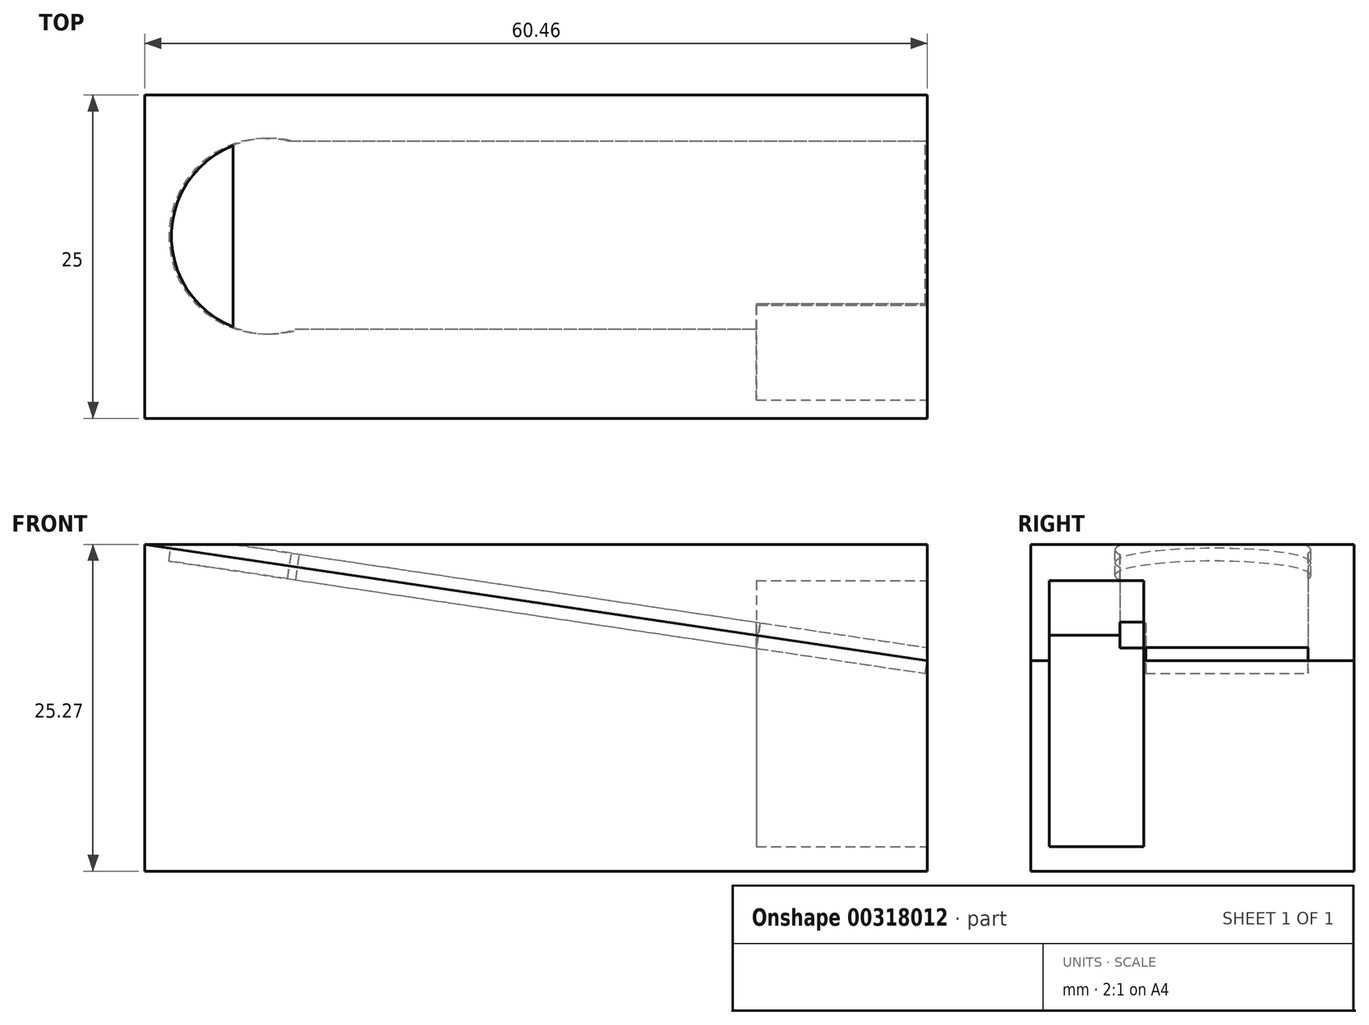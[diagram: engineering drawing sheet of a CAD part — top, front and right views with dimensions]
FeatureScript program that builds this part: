
annotation { "Feature Type Name" : "Feature", "Feature Type Description" : "" }
export const myFeature = defineFeature(function(context is Context, id is Id, definition is map)
    precondition{}
    {
        {
            var Q0;
            Q0=qCreatedBy(makeId("Front.planeOp"),FACE);
            var sketch = newSketch(context, id + "F0", { "sketchPlane" : qUnion([Q0])});
            skLineSegment(sketch, "E0.bottom", {"start": v(0, 0) * mm, "end": v(-60.46, 0) * mm});
            skLineSegment(sketch, "E0.top", {"start": v(0, 25.27) * mm, "end": v(-60.46, 25.27) * mm});
            skLineSegment(sketch, "E0.left", {"start": v(0, 0) * mm, "end": v(0, 25.27) * mm});
            skLineSegment(sketch, "E0.right", {"start": v(-60.46, 0) * mm, "end": v(-60.46, 25.27) * mm});
            skSolve(sketch);
        }
        {
            var Q0;
            Q0=makeQuery(id+"F0.imprint","IMPRINT",FACE,{"disambiguationData":[TD([[makeQuery(id+"F0.imprint","IMPRINT",EDGE,{"derivedFrom":sQuery(id+"F0.wireOp",EDGE,"E0.bottom")}),-1.0]])]});
            extrude(context, id + "F1", {"entities" : qUnion([Q0]), "depth" : 25 * mm});
        }
        {
            var Q0;
            Q0=makeQuery(id+"F1.opExtrude","SWEPT_FACE",FACE,{"disambiguationData":[OSD([sQuery(id+"F0.wireOp",EDGE,"E0.left")])]});
            var sketch = newSketch(context, id + "F2", { "sketchPlane" : qUnion([Q0])});
            skLineSegment(sketch, "E1.bottom", {"start": v(-25, 16.28) * mm, "end": v(0, 16.28) * mm});
            skLineSegment(sketch, "E1.top", {"start": v(-25, 0) * mm, "end": v(0, 0) * mm});
            skLineSegment(sketch, "E1.left", {"start": v(-25, 16.28) * mm, "end": v(-25, 0) * mm});
            skLineSegment(sketch, "E1.right", {"start": v(0, 16.28) * mm, "end": v(0, 0) * mm});
            skSolve(sketch);
        }
        {
            var Q0;
            Q0=makeQuery(id+"F1.opExtrude","SWEPT_FACE",FACE,{"disambiguationData":[OSD([sQuery(id+"F0.wireOp",EDGE,"E0.right")])]});
            var sketch = newSketch(context, id + "F3", { "sketchPlane" : qUnion([Q0])});
            skLineSegment(sketch, "E2.bottom", {"start": v(0, 25.27) * mm, "end": v(25, 25.27) * mm});
            skLineSegment(sketch, "E2.top", {"start": v(0, 0) * mm, "end": v(25, 0) * mm});
            skLineSegment(sketch, "E2.left", {"start": v(0, 25.27) * mm, "end": v(0, 0) * mm});
            skLineSegment(sketch, "E2.right", {"start": v(25, 25.27) * mm, "end": v(25, 0) * mm});
            skSolve(sketch);
        }
        {
            var Q1;
            Q1 = qSketchRegion(id + "F2", true);
            var Q2;
            Q2 = qSketchRegion(id + "F3", true);
            loft(context, id + "F4", {"sheetProfilesArray" : [{ "sheetProfileEntities" : qUnion([Q1]) }, { "sheetProfileEntities" : qUnion([Q2]) }]});
        }
        {
            var Q0;
            Q0=makeQuery(id+"F4.opLoft","SWEPT_FACE",FACE,{"disambiguationData":[OSD([sQuery(id+"F0.wireOp",EDGE,"E0.left"),sQuery(id+"F2.wireOp",EDGE,"E1.bottom"),sQuery(id+"F2.wireOp",EDGE,"E1.left"),sQuery(id+"F2.wireOp",EDGE,"E1.right"),sQuery(id+"F3.wireOp",EDGE,"E2.bottom"),sQuery(id+"F3.wireOp",EDGE,"E2.left"),sQuery(id+"F3.wireOp",EDGE,"E2.right")])]});
            var sketch = newSketch(context, id + "F5", { "sketchPlane" : qUnion([Q0])});
            skArc(sketch, "E3", {"start": v(-52.21, -3.54) * mm, "mid": v(-61.5, -11.24) * mm, "end": v(-51.58, -18.1) * mm});
            skLineSegment(sketch, "E4", {"start": v(-52.21, -3.54) * mm, "end": v(-2.4, -3.54) * mm});
            skLineSegment(sketch, "E5", {"start": v(-51.58, -18.1) * mm, "end": v(-15.6, -18.1) * mm});
            skLineSegment(sketch, "E6", {"start": v(-15.6, -18.1) * mm, "end": v(-15.6, -16.11) * mm});
            skLineSegment(sketch, "E7", {"start": v(-15.6, -16.11) * mm, "end": v(-2.4, -16.11) * mm});
            skSolve(sketch);
        }
        {
            var Q0;
            Q0=makeQuery(id+"F5.imprint","IMPRINT",FACE,{"disambiguationData":[TD([[makeQuery(id+"F5.imprint","IMPRINT",EDGE,{"derivedFrom":sQuery(id+"F5.wireOp",EDGE,"E3")}),1.0]])]});
            extrude(context, id + "F6", {"entities" : qUnion([Q0]), "operationType" : NewBodyOperationType.REMOVE, "endBound" : BoundingType.SYMMETRIC, "oppositeDirection" : true, "depth" : 2 * mm});
        }
        {
            var Q0;
            Q0=qCreatedBy(makeId("Right.planeOp"),FACE);
            var sketch = newSketch(context, id + "F7", { "sketchPlane" : qUnion([Q0])});
            skLineSegment(sketch, "E8.bottom", {"start": v(-16.26, 22.48) * mm, "end": v(-23.57, 22.48) * mm});
            skLineSegment(sketch, "E8.top", {"start": v(-16.26, 1.89) * mm, "end": v(-23.57, 1.89) * mm});
            skLineSegment(sketch, "E8.left", {"start": v(-16.26, 22.48) * mm, "end": v(-16.26, 1.89) * mm});
            skLineSegment(sketch, "E8.right", {"start": v(-23.57, 22.48) * mm, "end": v(-23.57, 1.89) * mm});
            skSolve(sketch);
        }
        {
            var Q0;
            Q0=makeQuery(id+"F7.imprint","IMPRINT",FACE,{"disambiguationData":[TD([[makeQuery(id+"F7.imprint","IMPRINT",EDGE,{"derivedFrom":sQuery(id+"F7.wireOp",EDGE,"E8.bottom")}),1.0]])]});
            extrude(context, id + "F8", {"entities" : qUnion([Q0]), "operationType" : NewBodyOperationType.REMOVE, "oppositeDirection" : true, "depth" : 13.2 * mm});
        }
    });
